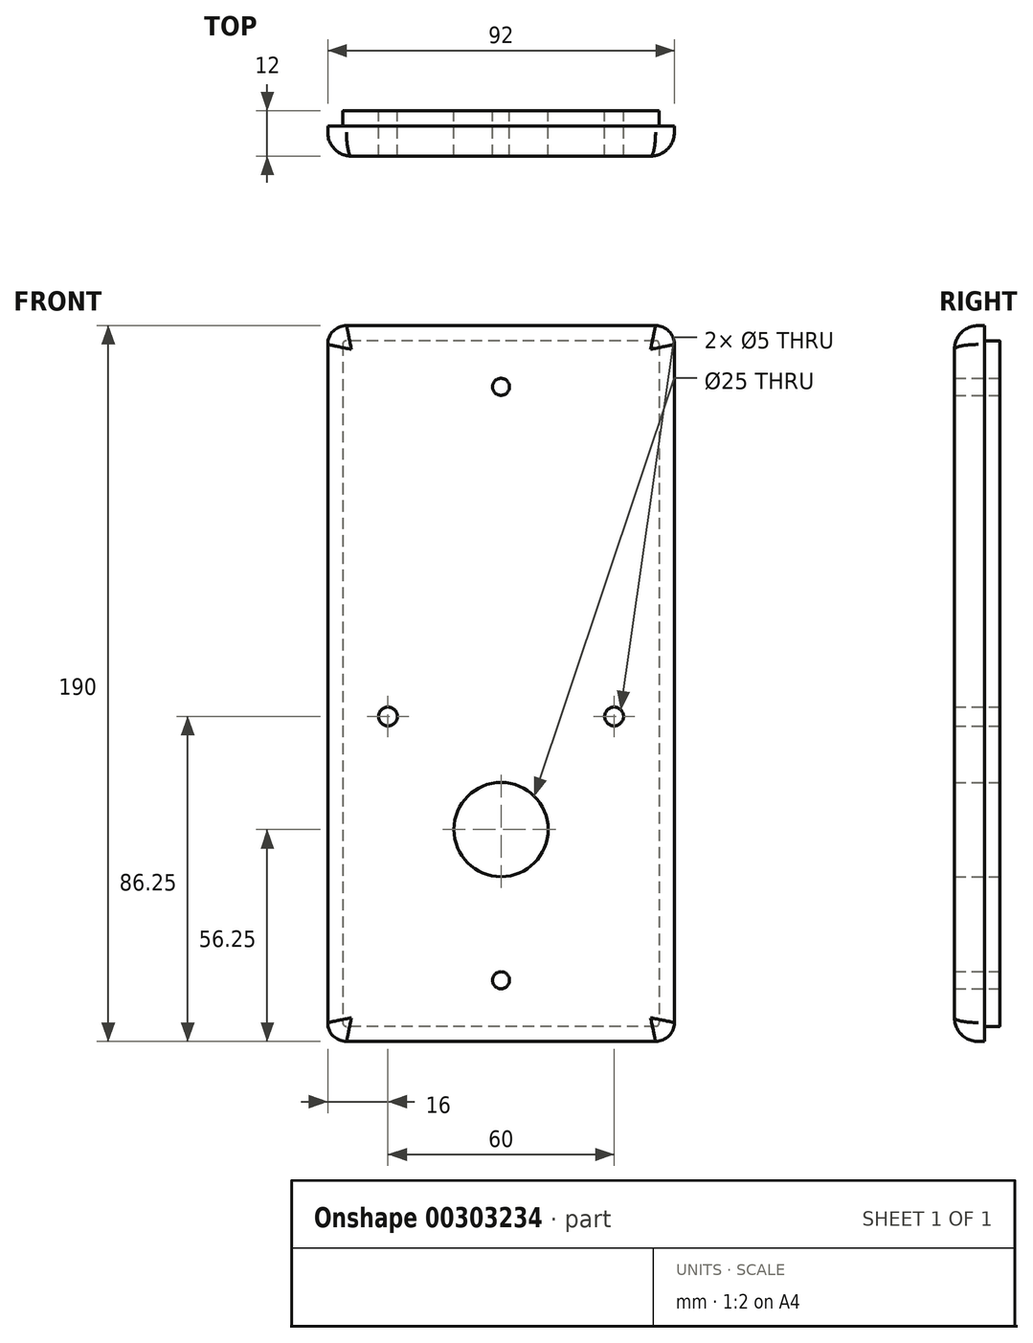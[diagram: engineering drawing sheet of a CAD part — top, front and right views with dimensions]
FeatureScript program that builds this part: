
annotation { "Feature Type Name" : "Feature", "Feature Type Description" : "" }
export const myFeature = defineFeature(function(context is Context, id is Id, definition is map)
    precondition{}
    {
        {
            var Q0;
            Q0=qCreatedBy(makeId("Front.planeOp"),FACE);
            var sketch = newSketch(context, id + "F0", { "sketchPlane" : qUnion([Q0])});
            skLineSegment(sketch, "E0.bottom", {"start": v(41, 95) * mm, "end": v(-41, 95) * mm});
            skLineSegment(sketch, "E0.top", {"start": v(41, -95) * mm, "end": v(-41, -95) * mm});
            skLineSegment(sketch, "E0.left", {"start": v(46, 90) * mm, "end": v(46, -90) * mm});
            skLineSegment(sketch, "E0.right", {"start": v(-46, 90) * mm, "end": v(-46, -90) * mm});
            skPoint(sketch, "E0.middle", {"position": v(0, 0) * mm});
            skPoint(sketch, "E1.visualSharp", {"position": v(46, 95) * mm});
            skArc(sketch, "E1.filletArc", {"start": v(46, 90) * mm, "mid": v(44.54, 93.54) * mm, "end": v(41, 95) * mm});
            skPoint(sketch, "E2.visualSharp", {"position": v(46, -95) * mm});
            skArc(sketch, "E2.filletArc", {"start": v(41, -95) * mm, "mid": v(44.54, -93.54) * mm, "end": v(46, -90) * mm});
            skPoint(sketch, "E3.visualSharp", {"position": v(-46, -95) * mm});
            skArc(sketch, "E3.filletArc", {"start": v(-46, -90) * mm, "mid": v(-44.54, -93.54) * mm, "end": v(-41, -95) * mm});
            skPoint(sketch, "E4.visualSharp", {"position": v(-46, 95) * mm});
            skArc(sketch, "E4.filletArc", {"start": v(-41, 95) * mm, "mid": v(-44.54, 93.54) * mm, "end": v(-46, 90) * mm});
            skCircle(sketch, "E5", {"center": v(0, 78.75) * mm, "radius": 2.25 * mm});
            skCircle(sketch, "E6", {"center": v(0, -78.75) * mm, "radius": 2.25 * mm});
            skLineSegment(sketch, "E7", {"start": v(0, 78.75) * mm, "end": v(0, 0) * mm, "construction": true});
            skLineSegment(sketch, "E8", {"start": v(0, 0) * mm, "end": v(0, -78.75) * mm, "construction": true});
            skCircle(sketch, "E9", {"center": v(0, -38.75) * mm, "radius": 12.5 * mm});
            skCircle(sketch, "E10", {"center": v(-30, -8.75) * mm, "radius": 2.5 * mm});
            skCircle(sketch, "E11", {"center": v(30, -8.75) * mm, "radius": 2.5 * mm});
            skLineSegment(sketch, "E12", {"start": v(-30, -8.75) * mm, "end": v(30, -8.75) * mm, "construction": true});
            skSolve(sketch);
        }
        {
            var Q0;
            Q0=makeQuery(id+"F0.imprint","IMPRINT",FACE,{"disambiguationData":[TD([[makeQuery(id+"F0.imprint","IMPRINT",EDGE,{"derivedFrom":sQuery(id+"F0.wireOp",EDGE,"E0.bottom")}),1.0]])]});
            extrude(context, id + "F1", {"entities" : qUnion([Q0]), "depth" : 12 * mm});
        }
        {
            var Q0;
            Q0=makeQuery(id+"F1.opExtrude","CAP_EDGE",EDGE,{"disambiguationData":[OSD([sQuery(id+"F0.wireOp",EDGE,"E0.left")])],"isStart":false});
            fillet(context, id + "F2", {"entities" : qUnion([Q0]), "radius" : 6.3 * mm, "tangentPropagation" : true, "allowEdgeOverflow" : false});
        }
        {
            var Q0;
            Q0=makeQuery(id+"F1.opExtrude","CAP_FACE",FACE,{"disambiguationData":[OSD([sQuery(id+"F0.wireOp",EDGE,"E0.bottom"),sQuery(id+"F0.wireOp",EDGE,"E0.top"),sQuery(id+"F0.wireOp",EDGE,"E0.left"),sQuery(id+"F0.wireOp",EDGE,"E0.right"),sQuery(id+"F0.wireOp",EDGE,"E1.filletArc"),sQuery(id+"F0.wireOp",EDGE,"E2.filletArc"),sQuery(id+"F0.wireOp",EDGE,"E3.filletArc"),sQuery(id+"F0.wireOp",EDGE,"E4.filletArc"),sQuery(id+"F0.wireOp",EDGE,"E5"),sQuery(id+"F0.wireOp",EDGE,"E6")])],"isStart":true});
            var sketch = newSketch(context, id + "F3", { "sketchPlane" : qUnion([Q0])});
            skArc(sketch, "E13.0", {"start": v(-42, 90) * mm, "mid": v(-41.7, 90.7) * mm, "end": v(-41, 91) * mm});
            skLineSegment(sketch, "E13.1", {"start": v(-42, 90) * mm, "end": v(-42, -90) * mm});
            skLineSegment(sketch, "E13.2", {"start": v(-41, 91) * mm, "end": v(41, 91) * mm});
            skArc(sketch, "E13.3", {"start": v(-41, -91) * mm, "mid": v(-41.7, -90.7) * mm, "end": v(-42, -90) * mm});
            skArc(sketch, "E13.4", {"start": v(41, 91) * mm, "mid": v(41.7, 90.7) * mm, "end": v(42, 90) * mm});
            skLineSegment(sketch, "E13.5", {"start": v(42, 90) * mm, "end": v(42, -90) * mm});
            skArc(sketch, "E13.6", {"start": v(42, -90) * mm, "mid": v(41.7, -90.7) * mm, "end": v(41, -91) * mm});
            skLineSegment(sketch, "E13.7", {"start": v(-41, -91) * mm, "end": v(41, -91) * mm});
            skSolve(sketch);
        }
        {
            var Q0;
            Q0=makeQuery(id+"F3.imprint","IMPRINT",FACE,{"disambiguationData":[TD([[makeQuery(id+"F3.imprint","IMPRINT",EDGE,{"derivedFrom":sQuery(id+"F3.wireOp",EDGE,"E13.0")}),-1.0]])]});
            extrude(context, id + "F4", {"entities" : qUnion([Q0]), "operationType" : NewBodyOperationType.REMOVE, "oppositeDirection" : true, "depth" : 4 * mm});
        }
    });
